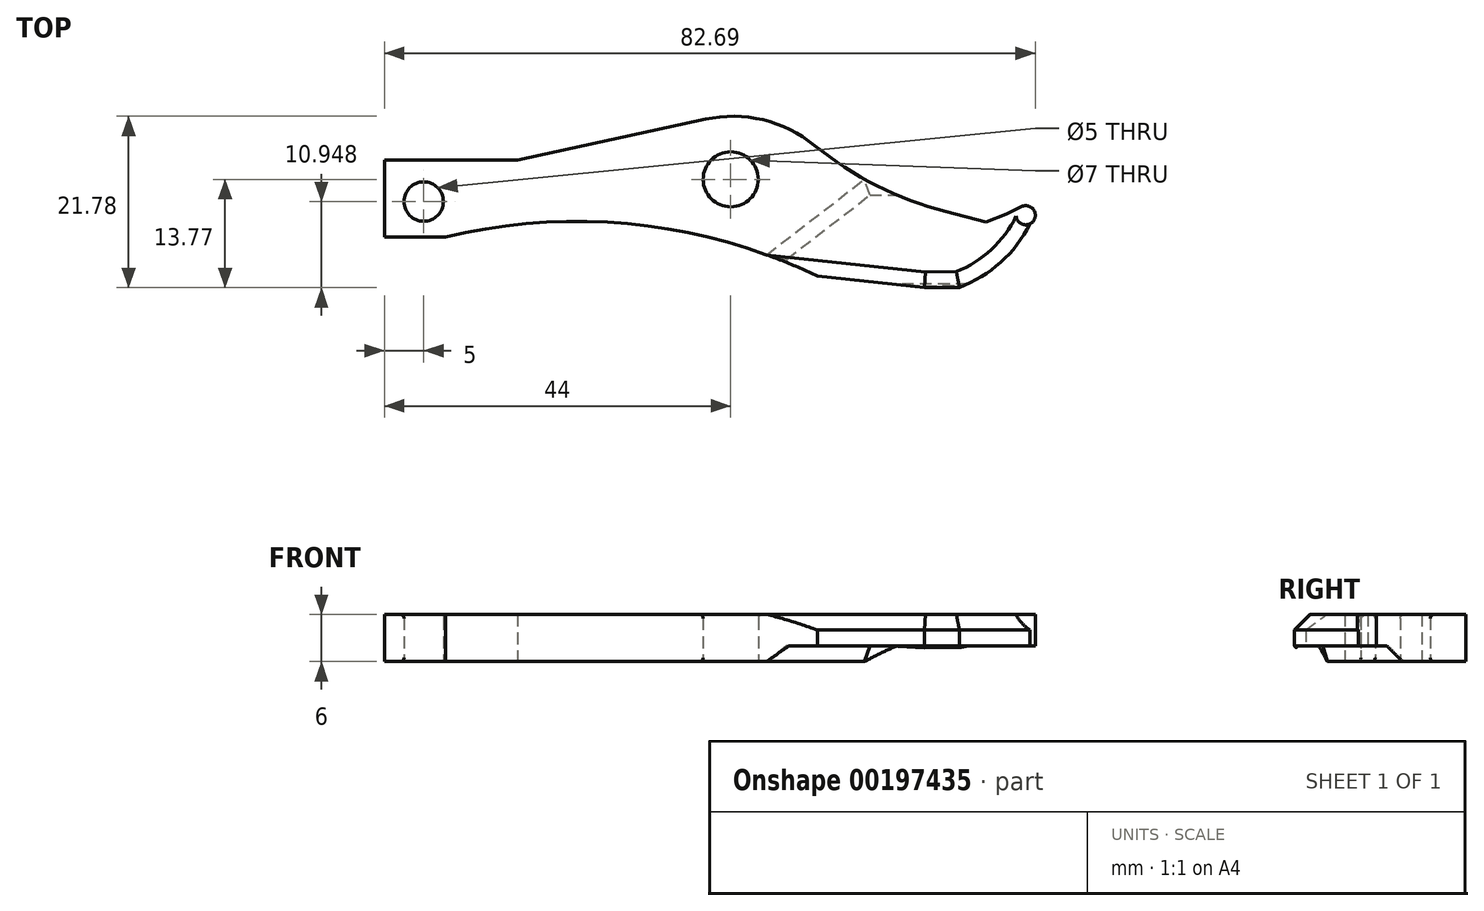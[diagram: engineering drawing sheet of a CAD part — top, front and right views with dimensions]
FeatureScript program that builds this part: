
annotation { "Feature Type Name" : "Feature", "Feature Type Description" : "" }
export const myFeature = defineFeature(function(context is Context, id is Id, definition is map)
    precondition{}
    {
        {
            var Q0;
            Q0=qCreatedBy(makeId("Top.planeOp"),FACE);
            var sketch = newSketch(context, id + "F0", { "sketchPlane" : qUnion([Q0])});
            skLineSegment(sketch, "E0", {"start": v(-39.56, 2.42) * mm, "end": v(-39.56, -7.33) * mm});
            skLineSegment(sketch, "E1", {"start": v(-39.56, -7.33) * mm, "end": v(-31.81, -7.33) * mm});
            skArc(sketch, "E2", {"start": v(15.46, -12.3) * mm, "mid": v(-7.75, -5.73) * mm, "end": v(-31.81, -7.33) * mm});
            skLineSegment(sketch, "E3", {"start": v(15.46, -12.3) * mm, "end": v(29.05, -13.77) * mm});
            skLineSegment(sketch, "E4", {"start": v(29.05, -13.77) * mm, "end": v(33.48, -13.73) * mm});
            skArc(sketch, "E5", {"start": v(33.48, -13.73) * mm, "mid": v(38.72, -10.54) * mm, "end": v(42.44, -5.66) * mm});
            skPoint(sketch, "E5.endSnap0", {"position": v(43.66, -5.66) * mm});
            skLineSegment(sketch, "E6", {"start": v(-39.56, 2.42) * mm, "end": v(-22.66, 2.42) * mm});
            skLineSegment(sketch, "E7", {"start": v(-22.66, 2.42) * mm, "end": v(1.2, 7.63) * mm});
            skArc(sketch, "E8", {"start": v(15.1, 4.32) * mm, "mid": v(8.53, 7.56) * mm, "end": v(1.2, 7.63) * mm});
            skArc(sketch, "E9", {"start": v(15.1, 4.32) * mm, "mid": v(22.97, -0.82) * mm, "end": v(31.78, -4.12) * mm});
            skLineSegment(sketch, "E10", {"start": v(39.44, -4.4) * mm, "end": v(41.38, -3.47) * mm});
            skArc(sketch, "E11", {"start": v(42.44, -5.66) * mm, "mid": v(43, -4.04) * mm, "end": v(41.38, -3.47) * mm});
            skLineSegment(sketch, "E12", {"start": v(36.85, -5.4) * mm, "end": v(39.44, -4.4) * mm});
            skCircle(sketch, "E13", {"center": v(-34.56, -2.82) * mm, "radius": 2.5 * mm});
            skCircle(sketch, "E14", {"center": v(-34.56, -2.82) * mm, "radius": 3.37 * mm, "construction": true});
            skCircle(sketch, "E15", {"center": v(4.44, 0) * mm, "radius": 3.5 * mm});
            skCircle(sketch, "E16", {"center": v(4.44, 0) * mm, "radius": 4.5 * mm, "construction": true});
            skLineSegment(sketch, "E17", {"start": v(-39.56, -7.33) * mm, "end": v(-39.56, 54.57) * mm, "construction": true});
            skLineSegment(sketch, "E18", {"start": v(-39.56, -7.33) * mm, "end": v(43.66, -7.33) * mm, "construction": true});
            skLineSegment(sketch, "E19", {"start": v(31.78, -4.12) * mm, "end": v(36.85, -5.4) * mm});
            skSolve(sketch);
        }
        {
            var Q0;
            Q0 = qSketchRegion(id + "F0", true);
            extrude(context, id + "F1", {"entities" : qUnion([Q0]), "endBound" : BoundingType.SYMMETRIC, "depth" : 6 * mm});
        }
        {
            var Q0;
            Q0=makeQuery(id+"F1.opExtrude","CAP_EDGE",EDGE,{"disambiguationData":[OSD([sQuery(id+"F0.wireOp",EDGE,"E3")])],"isStart":false});
            var Q1;
            Q1=makeQuery(id+"F1.opExtrude","CAP_EDGE",EDGE,{"disambiguationData":[OSD([sQuery(id+"F0.wireOp",EDGE,"E3")])],"isStart":true});
            var Q2;
            Q2=makeQuery(id+"F1.opExtrude","CAP_EDGE",EDGE,{"disambiguationData":[OSD([sQuery(id+"F0.wireOp",EDGE,"E4")])],"isStart":false});
            var Q3;
            Q3=makeQuery(id+"F1.opExtrude","CAP_EDGE",EDGE,{"disambiguationData":[OSD([sQuery(id+"F0.wireOp",EDGE,"E4")])],"isStart":true});
            var Q4;
            Q4=makeQuery(id+"F1.opExtrude","CAP_EDGE",EDGE,{"disambiguationData":[OSD([sQuery(id+"F0.wireOp",EDGE,"E5")])],"isStart":false});
            var Q5;
            Q5=makeQuery(id+"F1.opExtrude","CAP_EDGE",EDGE,{"disambiguationData":[OSD([sQuery(id+"F0.wireOp",EDGE,"E5")])],"isStart":true});
            chamfer(context, id + "F2", {"entities" : qUnion([Q0, Q1, Q2, Q3, Q4, Q5]), "width" : 2 * mm, "tangentPropagation" : true});
        }
        {
            var Q0;
            Q0=makeQuery(id+"F1.opExtrude","CAP_FACE",FACE,{"disambiguationData":[OSD([sQuery(id+"F0.wireOp",EDGE,"E0"),sQuery(id+"F0.wireOp",EDGE,"E1"),sQuery(id+"F0.wireOp",EDGE,"E2"),sQuery(id+"F0.wireOp",EDGE,"E3"),sQuery(id+"F0.wireOp",EDGE,"E4"),sQuery(id+"F0.wireOp",EDGE,"E5"),sQuery(id+"F0.wireOp",EDGE,"E6"),sQuery(id+"F0.wireOp",EDGE,"E7"),sQuery(id+"F0.wireOp",EDGE,"E8"),sQuery(id+"F0.wireOp",EDGE,"E9"),sQuery(id+"F0.wireOp",EDGE,"E10"),sQuery(id+"F0.wireOp",EDGE,"E11"),sQuery(id+"F0.wireOp",EDGE,"5MSSyLMy-xGv9-1TTs-lDIS-RehOosuFGkv6"),sQuery(id+"F0.wireOp",EDGE,"UzA5vFTT-ODsB-QiHi-Abpz-L10IxV0yyN0J"),sQuery(id+"F0.wireOp",EDGE,"E12"),sQuery(id+"F0.wireOp",EDGE,"E13"),sQuery(id+"F0.wireOp",EDGE,"E15")])],"isStart":true});
            var sketch = newSketch(context, id + "F3", { "sketchPlane" : qUnion([Q0])});
            skLineSegment(sketch, "E20", {"start": v(9, 9.59) * mm, "end": v(21.44, 0) * mm});
            skLineSegment(sketch, "E21", {"start": v(21.44, 0) * mm, "end": v(52.89, 0) * mm});
            skLineSegment(sketch, "E22", {"start": v(52.89, 0) * mm, "end": v(52.89, 15.28) * mm});
            skLineSegment(sketch, "E23", {"start": v(52.89, 15.28) * mm, "end": v(11.92, 15.28) * mm});
            skLineSegment(sketch, "E24", {"start": v(11.92, 15.28) * mm, "end": v(9, 9.59) * mm});
            skSolve(sketch);
        }
        {
            var Q0;
            Q0=makeQuery(id+"F1.opExtrude","CAP_EDGE",EDGE,{"disambiguationData":[OSD([sQuery(id+"F0.wireOp",EDGE,"E15")])],"isStart":true});
            var Q1;
            Q1=makeQuery(id+"F1.opExtrude","CAP_EDGE",EDGE,{"disambiguationData":[OSD([sQuery(id+"F0.wireOp",EDGE,"E13")])],"isStart":true});
            var Q2;
            Q2=makeQuery(id+"F1.opExtrude","CAP_EDGE",EDGE,{"disambiguationData":[OSD([sQuery(id+"F0.wireOp",EDGE,"E13")])],"isStart":false});
            var Q3;
            Q3=makeQuery(id+"F1.opExtrude","CAP_EDGE",EDGE,{"disambiguationData":[OSD([sQuery(id+"F0.wireOp",EDGE,"E15")])],"isStart":false});
            fillet(context, id + "F4", {"entities" : qUnion([Q0, Q1, Q2, Q3]), "radius" : .5 * mm, "tangentPropagation" : true, "allowEdgeOverflow" : false});
        }
        {
            var Q0;
            Q0 = qSketchRegion(id + "F3", true);
            extrude(context, id + "F5", {"entities" : qUnion([Q0]), "operationType" : NewBodyOperationType.REMOVE, "oppositeDirection" : true, "depth" : 2 * mm, "hasDraft" : true, "draftAngle" : 45 * degree, "draftPullDirection" : true});
        }
    });
